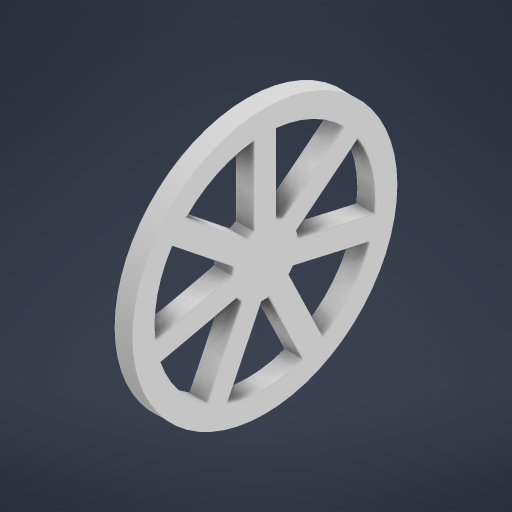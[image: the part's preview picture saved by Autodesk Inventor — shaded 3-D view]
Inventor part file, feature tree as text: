
AUTODESK INVENTOR PART (.ipt)
format: ipt  version: 2023.2 (Build 272271000, 271)  size: 335,360 bytes
history: native  units: mm
features: sketch x2
ambient origin geometry x8: Origin, YZ Plane, XZ Plane, XY Plane, X Axis, Y Axis, Z Axis, Center Point
bodies: Body1 (feature_tree)
feature tree (2):
  sketch  "Sketch1"  dims[d228=60.0mm]
  sketch  "Sketch3"  dims[d229=4.0mm d230=0.0mm d251=15.0mm d252=5.0mm d257=4.0mm d258=0.0mm d259=5.0mm d260=70.0mm d262=360.0deg d9=0.5mm d10=0.872665mm d11=0.5mm d12=0.872665mm d13=0.5mm d14=0.872665mm d27=0.5mm d28=0.872665mm d29=0.5mm d30=0.872665mm d88=0.5mm d89=0.872665mm d90=0.5mm d91=0.872665mm d116=0.5mm d117=0.872665mm d118=0.5mm d119=0.872665mm d154=0.5mm d155=0.872665mm d156=0.5mm d157=0.872665mm d181=0.5mm d182=0.872665mm d183=0.5mm d184=0.872665mm d221=0.5mm d222=0.872665mm d223=0.5mm d224=0.872665mm]
